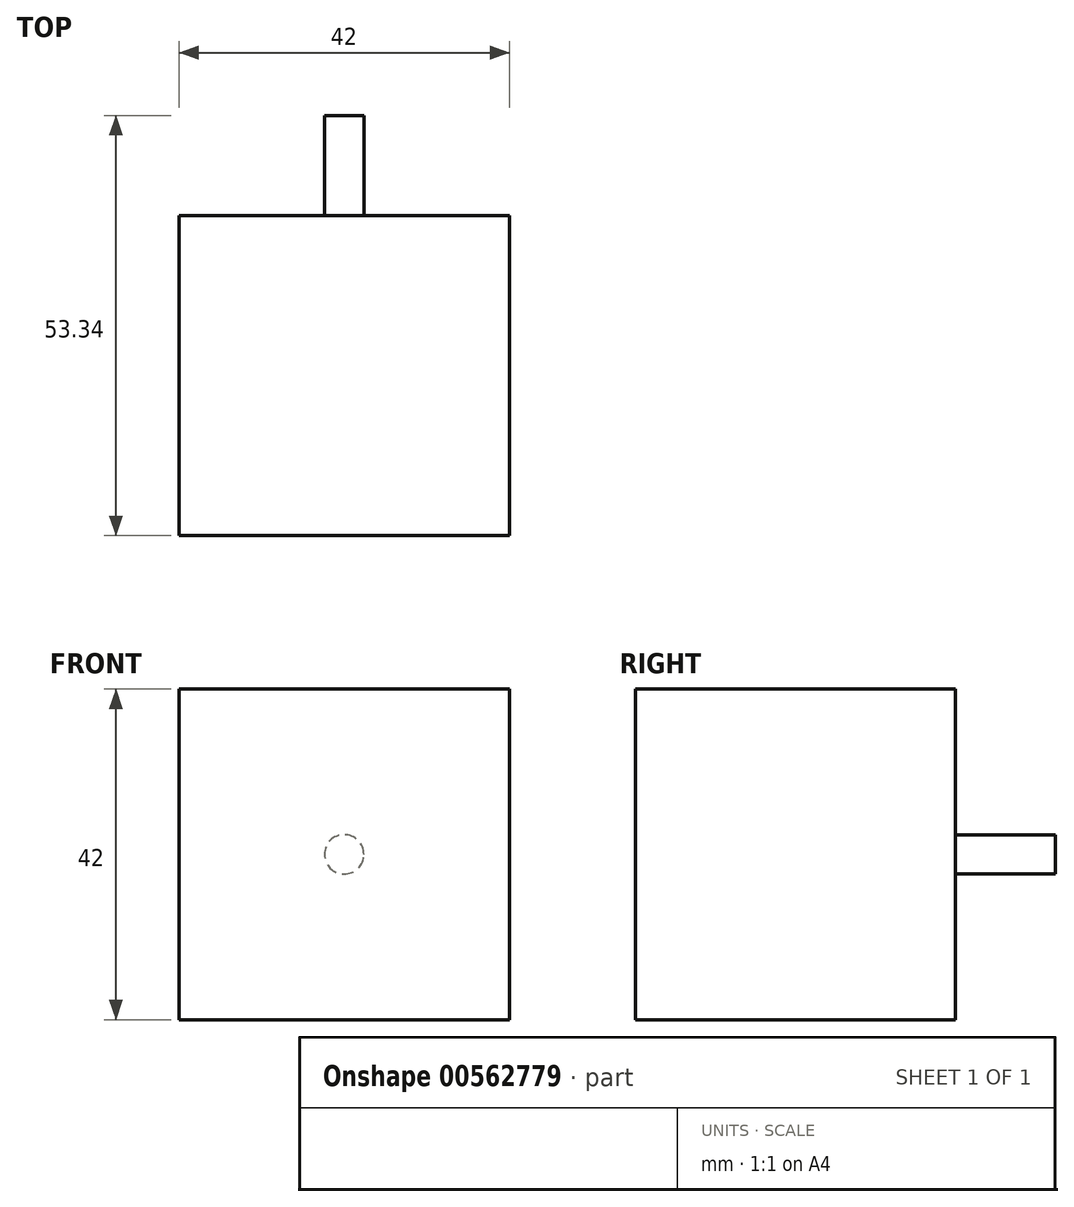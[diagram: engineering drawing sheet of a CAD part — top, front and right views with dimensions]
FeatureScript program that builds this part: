
annotation { "Feature Type Name" : "Feature", "Feature Type Description" : "" }
export const myFeature = defineFeature(function(context is Context, id is Id, definition is map)
    precondition{}
    {
        {
            var Q0;
            Q0=qCreatedBy(makeId("Front.planeOp"),FACE);
            var sketch = newSketch(context, id + "F0", { "sketchPlane" : qUnion([Q0])});
            skLineSegment(sketch, "E0.bottom", {"start": v(-21, 21) * mm, "end": v(21, 21) * mm});
            skLineSegment(sketch, "E0.top", {"start": v(-21, -21) * mm, "end": v(21, -21) * mm});
            skLineSegment(sketch, "E0.left", {"start": v(-21, 21) * mm, "end": v(-21, -21) * mm});
            skLineSegment(sketch, "E0.right", {"start": v(21, 21) * mm, "end": v(21, -21) * mm});
            skPoint(sketch, "E0.middle", {"position": v(0, 0) * mm});
            skSolve(sketch);
        }
        {
            var Q0;
            Q0 = qSketchRegion(id + "F0", true);
            extrude(context, id + "F1", {"entities" : qUnion([Q0]), "depth" : 40.64 * mm, "offsetDistance" : 25.4 * mm});
        }
        {
            var Q0;
            Q0=makeQuery(id+"F1.opExtrude","CAP_FACE",FACE,{"disambiguationData":[OSD([sQuery(id+"F0.wireOp",EDGE,"E0.bottom"),sQuery(id+"F0.wireOp",EDGE,"E0.top"),sQuery(id+"F0.wireOp",EDGE,"E0.left"),sQuery(id+"F0.wireOp",EDGE,"E0.right")])],"isStart":true});
            var sketch = newSketch(context, id + "F2", { "sketchPlane" : qUnion([Q0])});
            skCircle(sketch, "E1", {"center": v(0, 0) * mm, "radius": 2.5 * mm});
            skSolve(sketch);
        }
        {
            var Q0;
            Q0 = qSketchRegion(id + "F2", true);
            extrude(context, id + "F3", {"entities" : qUnion([Q0]), "operationType" : NewBodyOperationType.ADD, "depth" : 12.7 * mm, "offsetDistance" : 25.4 * mm});
        }
    });
